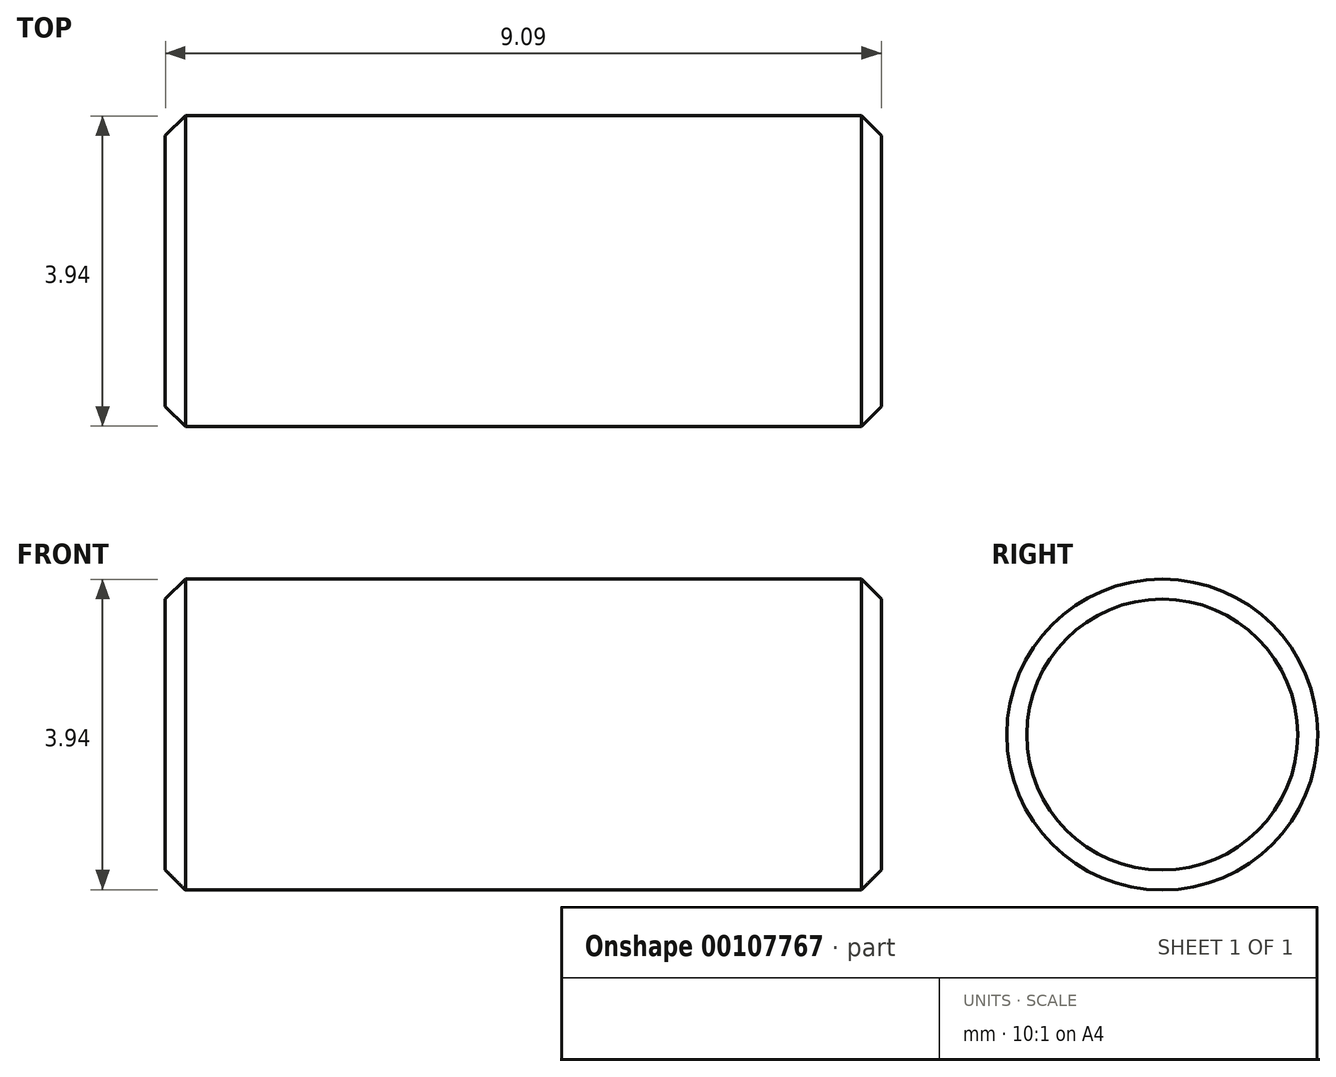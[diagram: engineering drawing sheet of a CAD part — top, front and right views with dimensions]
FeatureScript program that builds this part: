
annotation { "Feature Type Name" : "Feature", "Feature Type Description" : "" }
export const myFeature = defineFeature(function(context is Context, id is Id, definition is map)
    precondition{}
    {
        {
            var Q0;
            Q0=qCreatedBy(makeId("Right.planeOp"),FACE);
            var sketch = newSketch(context, id + "F0", { "sketchPlane" : qUnion([Q0])});
            skCircle(sketch, "E0", {"center": v(0, 0) * mm, "radius": 1.97 * mm});
            skSolve(sketch);
        }
        {
            var Q0;
            Q0=makeQuery(id+"F0.imprint","IMPRINT",FACE,{"disambiguationData":[TD([[makeQuery(id+"F0.imprint","IMPRINT",EDGE,{"derivedFrom":sQuery(id+"F0.wireOp",EDGE,"E0")}),1.0]])]});
            extrude(context, id + "F1", {"entities" : qUnion([Q0]), "oppositeDirection" : true, "depth" : 9.1 * mm});
        }
        {
            var Q0;
            Q0=makeQuery(id+"F1.opExtrude","CAP_EDGE",EDGE,{"disambiguationData":[OSD([sQuery(id+"F0.wireOp",EDGE,"E0")])],"isStart":true});
            chamfer(context, id + "F2", {"entities" : qUnion([Q0]), "chamferType" : ChamferType.OFFSET_ANGLE, "width" : 0.25 * mm, "oppositeDirection" : false, "angle" : 45 * degree, "tangentPropagation" : true});
        }
        {
            var Q0;
            Q0=makeQuery(id+"F1.opExtrude","CAP_EDGE",EDGE,{"disambiguationData":[OSD([sQuery(id+"F0.wireOp",EDGE,"E0")])],"isStart":false});
            chamfer(context, id + "F3", {"entities" : qUnion([Q0]), "chamferType" : ChamferType.OFFSET_ANGLE, "width" : 0.25 * mm, "oppositeDirection" : false, "angle" : 45 * degree, "tangentPropagation" : true});
        }
    });
